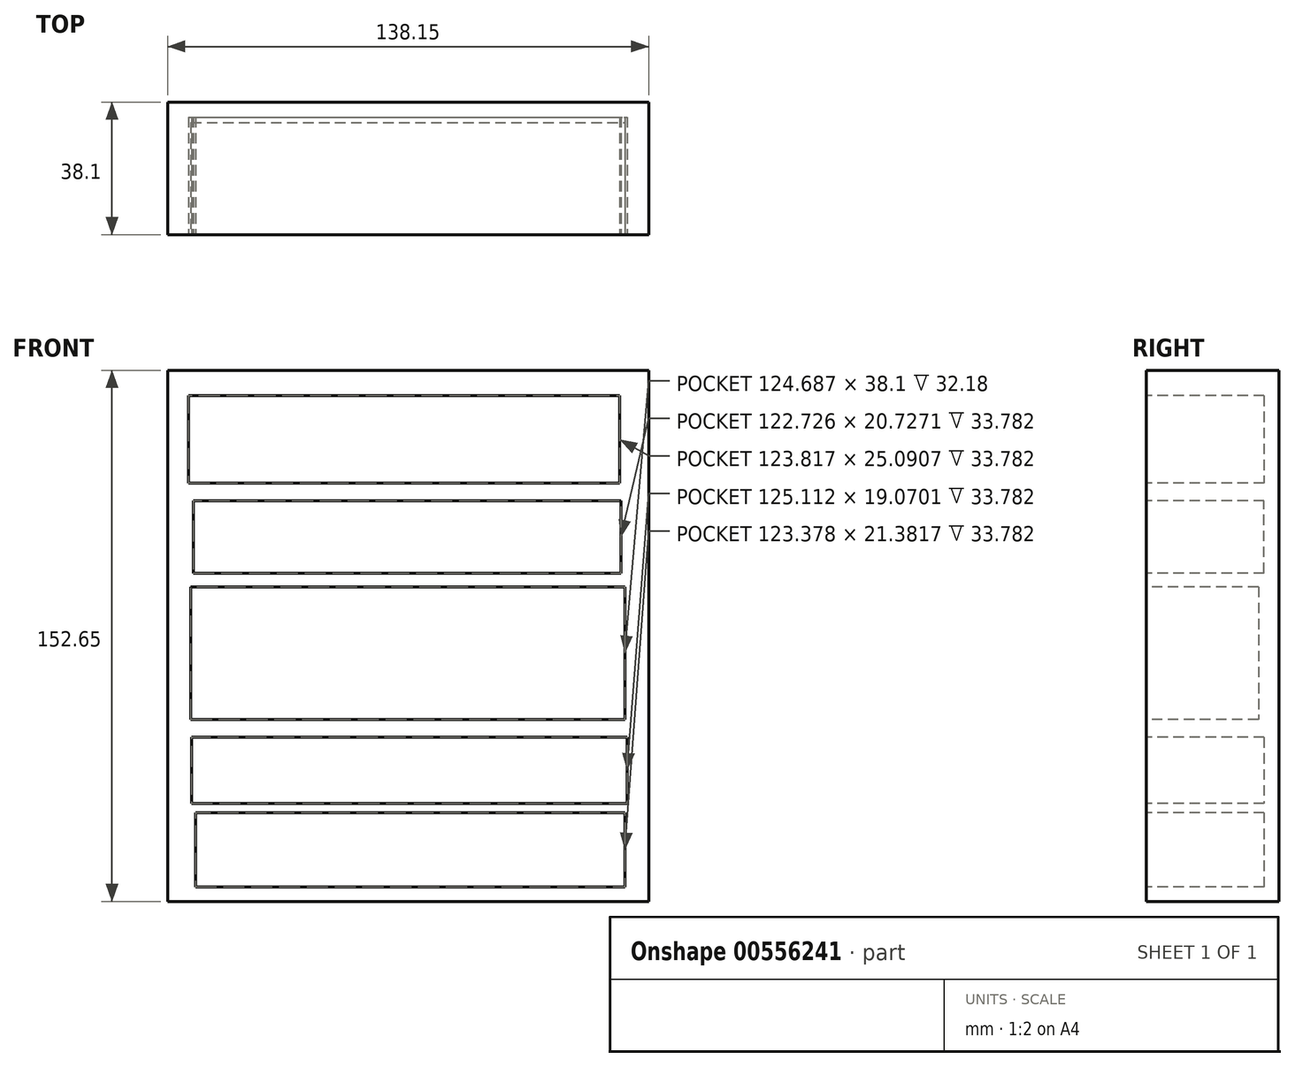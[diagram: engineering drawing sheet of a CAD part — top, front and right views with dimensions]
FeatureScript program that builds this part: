
annotation { "Feature Type Name" : "Feature", "Feature Type Description" : "" }
export const myFeature = defineFeature(function(context is Context, id is Id, definition is map)
    precondition{}
    {
        {
            var Q0;
            Q0=qCreatedBy(makeId("Front.planeOp"),FACE);
            var sketch = newSketch(context, id + "F0", { "sketchPlane" : qUnion([Q0])});
            skLineSegment(sketch, "E0.bottom", {"start": v(-68.66, 0) * mm, "end": v(69.49, 0) * mm});
            skLineSegment(sketch, "E0.top", {"start": v(-68.66, 52.32) * mm, "end": v(69.49, 52.32) * mm});
            skLineSegment(sketch, "E0.left", {"start": v(-68.66, 0) * mm, "end": v(-68.66, 52.32) * mm});
            skLineSegment(sketch, "E0.right", {"start": v(69.49, 0) * mm, "end": v(69.49, 52.32) * mm});
            skSolve(sketch);
        }
        {
            var Q0;
            Q0=makeQuery(id+"F0.imprint","IMPRINT",FACE,{"disambiguationData":[TD([[makeQuery(id+"F0.imprint","IMPRINT",EDGE,{"derivedFrom":sQuery(id+"F0.wireOp",EDGE,"E0.bottom")}),1.0]])]});
            var Q1;
            Q1 = qSketchRegion(id + "F2", true);
            extrude(context, id + "F1", {"entities" : qUnion([Q0, Q1]), "depth" : 38.1 * mm, "offsetDistance" : 25.4 * mm});
        }
        {
            var Q0;
            Q0=makeQuery(id+"F1.opExtrude","SWEPT_FACE",FACE,{"disambiguationData":[OSD([sQuery(id+"F0.wireOp",EDGE,"E0.top")])]});
            var sketch = newSketch(context, id + "F2", { "sketchPlane" : qUnion([Q0])});
            skLineSegment(sketch, "E1.bottom", {"start": v(-68.66, 0) * mm, "end": v(-61.96, 0) * mm});
            skLineSegment(sketch, "E1.top", {"start": v(-68.66, -38.1) * mm, "end": v(-61.96, -38.1) * mm});
            skLineSegment(sketch, "E1.left", {"start": v(-68.66, 0) * mm, "end": v(-68.66, -38.1) * mm});
            skLineSegment(sketch, "E1.right", {"start": v(-61.96, 0) * mm, "end": v(-61.96, -38.1) * mm});
            skLineSegment(sketch, "E2.bottom", {"start": v(69.49, 0) * mm, "end": v(62.73, 0) * mm});
            skLineSegment(sketch, "E2.top", {"start": v(69.49, -38.1) * mm, "end": v(62.73, -38.1) * mm});
            skLineSegment(sketch, "E2.left", {"start": v(69.49, 0) * mm, "end": v(69.49, -38.1) * mm});
            skLineSegment(sketch, "E2.right", {"start": v(62.73, 0) * mm, "end": v(62.73, -38.1) * mm});
            skLineSegment(sketch, "E3.bottom", {"start": v(-61.96, 0) * mm, "end": v(62.73, 0) * mm});
            skLineSegment(sketch, "E3.top", {"start": v(-61.96, -5.92) * mm, "end": v(62.73, -5.92) * mm});
            skLineSegment(sketch, "E3.left", {"start": v(-61.96, 0) * mm, "end": v(-61.96, -5.92) * mm});
            skLineSegment(sketch, "E3.right", {"start": v(62.73, 0) * mm, "end": v(62.73, -5.92) * mm});
            skSolve(sketch);
        }
        {
            var Q0;
            Q0 = qSketchRegion(id + "F2", true);
            extrude(context, id + "F3", {"entities" : qUnion([Q0]), "operationType" : NewBodyOperationType.ADD, "depth" : 38.1 * mm, "offsetDistance" : 25.4 * mm});
        }
        {
            var Q0;
            Q0=makeQuery(id+"F3.opExtrude","CAP_FACE",FACE,{"disambiguationData":[OSD([sQuery(id+"F2.wireOp",EDGE,"E1.bottom"),sQuery(id+"F2.wireOp",EDGE,"E1.top"),sQuery(id+"F2.wireOp",EDGE,"E1.left"),sQuery(id+"F2.wireOp",EDGE,"E1.right"),sQuery(id+"F2.wireOp",EDGE,"E2.bottom"),sQuery(id+"F2.wireOp",EDGE,"E2.top"),sQuery(id+"F2.wireOp",EDGE,"E2.left"),sQuery(id+"F2.wireOp",EDGE,"E2.right"),sQuery(id+"F2.wireOp",EDGE,"E3.bottom"),sQuery(id+"F2.wireOp",EDGE,"E3.top")])],"isStart":false});
            var sketch = newSketch(context, id + "F4", { "sketchPlane" : qUnion([Q0])});
            skLineSegment(sketch, "E4.bottom", {"start": v(-68.66, 0) * mm, "end": v(69.49, 0) * mm});
            skLineSegment(sketch, "E4.top", {"start": v(-68.66, -38.1) * mm, "end": v(69.49, -38.1) * mm});
            skLineSegment(sketch, "E4.left", {"start": v(-68.66, 0) * mm, "end": v(-68.66, -38.1) * mm});
            skLineSegment(sketch, "E4.right", {"start": v(69.49, 0) * mm, "end": v(69.49, -38.1) * mm});
            skSolve(sketch);
        }
        {
            var Q0;
            Q0 = qSketchRegion(id + "F4", true);
            extrude(context, id + "F5", {"entities" : qUnion([Q0]), "operationType" : NewBodyOperationType.ADD, "depth" : 2.54 * mm, "offsetDistance" : 25.4 * mm});
        }
        {
            var Q0;
            Q0=makeQuery(id+"F5.opExtrude","CAP_FACE",FACE,{"disambiguationData":[OSD([sQuery(id+"F4.wireOp",EDGE,"E4.bottom"),sQuery(id+"F4.wireOp",EDGE,"E4.top"),sQuery(id+"F4.wireOp",EDGE,"E4.left"),sQuery(id+"F4.wireOp",EDGE,"E4.right")])],"isStart":false});
            var sketch = newSketch(context, id + "F6", { "sketchPlane" : qUnion([Q0])});
            skLineSegment(sketch, "E5.bottom", {"start": v(-68.66, 0) * mm, "end": v(69.49, 0) * mm});
            skLineSegment(sketch, "E5.top", {"start": v(-68.66, -38.1) * mm, "end": v(69.49, -38.1) * mm});
            skLineSegment(sketch, "E5.left", {"start": v(-68.66, 0) * mm, "end": v(-68.66, -38.1) * mm});
            skLineSegment(sketch, "E5.right", {"start": v(69.49, 0) * mm, "end": v(69.49, -38.1) * mm});
            skSolve(sketch);
        }
        {
            var Q0;
            Q0 = qSketchRegion(id + "F6", true);
            extrude(context, id + "F7", {"entities" : qUnion([Q0]), "operationType" : NewBodyOperationType.ADD, "depth" : 59.69 * mm, "offsetDistance" : 25.4 * mm});
        }
        {
            var Q0;
            Q0=makeQuery(id+"F7.boolean.opBoolean","MERGE",FACE,{"derivedFrom":[makeQuery(id+"F5.boolean.opBoolean","MERGE",FACE,{"derivedFrom":[makeQuery(id+"F3.boolean.opBoolean","MERGE",FACE,{"derivedFrom":[makeQuery(id+"F1.opExtrude","CAP_FACE",FACE,{"disambiguationData":[OSD([sQuery(id+"F0.wireOp",EDGE,"E0.bottom"),sQuery(id+"F0.wireOp",EDGE,"E0.top"),sQuery(id+"F0.wireOp",EDGE,"E0.left"),sQuery(id+"F0.wireOp",EDGE,"E0.right")])],"isStart":false}),makeQuery(id+"F3.opExtrude","SWEPT_FACE",FACE,{"disambiguationData":[OSD([sQuery(id+"F2.wireOp",EDGE,"E1.top")])]}),makeQuery(id+"F3.opExtrude","SWEPT_FACE",FACE,{"disambiguationData":[OSD([sQuery(id+"F2.wireOp",EDGE,"E2.top")])]})]}),makeQuery(id+"F5.opExtrude","SWEPT_FACE",FACE,{"disambiguationData":[OSD([sQuery(id+"F4.wireOp",EDGE,"E4.top")])]})]}),makeQuery(id+"F7.opExtrude","SWEPT_FACE",FACE,{"disambiguationData":[OSD([sQuery(id+"F6.wireOp",EDGE,"E5.top")])]})]});
            var sketch = newSketch(context, id + "F8", { "sketchPlane" : qUnion([Q0])});
            skLineSegment(sketch, "E6.bottom", {"start": v(-61.24, 94.35) * mm, "end": v(61.49, 94.35) * mm});
            skLineSegment(sketch, "E6.top", {"start": v(-61.24, 115.08) * mm, "end": v(61.49, 115.08) * mm});
            skLineSegment(sketch, "E6.left", {"start": v(-61.24, 94.35) * mm, "end": v(-61.24, 115.08) * mm});
            skLineSegment(sketch, "E6.right", {"start": v(61.49, 94.35) * mm, "end": v(61.49, 115.08) * mm});
            skSolve(sketch);
        }
        {
            var Q0;
            Q0=makeQuery(id+"F8.imprint","IMPRINT",FACE,{"disambiguationData":[TD([[makeQuery(id+"F8.imprint","IMPRINT",EDGE,{"derivedFrom":sQuery(id+"F8.wireOp",EDGE,"E6.bottom")}),-1.0]])]});
            var sketch = newSketch(context, id + "F9", { "sketchPlane" : qUnion([Q0])});
            skLineSegment(sketch, "E7.bottom", {"start": v(-62.6, 145.35) * mm, "end": v(61.21, 145.35) * mm});
            skLineSegment(sketch, "E7.top", {"start": v(-62.6, 120.26) * mm, "end": v(61.21, 120.26) * mm});
            skLineSegment(sketch, "E7.left", {"start": v(-62.6, 145.35) * mm, "end": v(-62.6, 120.26) * mm});
            skLineSegment(sketch, "E7.right", {"start": v(61.21, 145.35) * mm, "end": v(61.21, 120.26) * mm});
            skSolve(sketch);
        }
        {
            var Q0;
            Q0=makeQuery(id+"F8.imprint","IMPRINT",FACE,{"disambiguationData":[TD([[makeQuery(id+"F8.imprint","IMPRINT",EDGE,{"derivedFrom":sQuery(id+"F8.wireOp",EDGE,"E6.bottom")}),-1.0]])]});
            var sketch = newSketch(context, id + "F10", { "sketchPlane" : qUnion([Q0])});
            skLineSegment(sketch, "E8.bottom", {"start": v(-61.8, 47.18) * mm, "end": v(63.3, 47.18) * mm});
            skLineSegment(sketch, "E8.top", {"start": v(-61.8, 28.1) * mm, "end": v(63.3, 28.1) * mm});
            skLineSegment(sketch, "E8.left", {"start": v(-61.8, 47.18) * mm, "end": v(-61.8, 28.1) * mm});
            skLineSegment(sketch, "E8.right", {"start": v(63.3, 47.18) * mm, "end": v(63.3, 28.1) * mm});
            skSolve(sketch);
        }
        {
            var Q0;
            Q0=makeQuery(id+"F8.imprint","IMPRINT",FACE,{"disambiguationData":[TD([[makeQuery(id+"F8.imprint","IMPRINT",EDGE,{"derivedFrom":sQuery(id+"F8.wireOp",EDGE,"E6.bottom")}),-1.0]])]});
            var sketch = newSketch(context, id + "F11", { "sketchPlane" : qUnion([Q0])});
            skLineSegment(sketch, "E9.bottom", {"start": v(-60.65, 25.5) * mm, "end": v(62.73, 25.5) * mm});
            skLineSegment(sketch, "E9.top", {"start": v(-60.65, 4.13) * mm, "end": v(62.73, 4.13) * mm});
            skLineSegment(sketch, "E9.left", {"start": v(-60.65, 25.5) * mm, "end": v(-60.65, 4.13) * mm});
            skLineSegment(sketch, "E9.right", {"start": v(62.73, 25.5) * mm, "end": v(62.73, 4.13) * mm});
            skSolve(sketch);
        }
        {
            var Q0;
            Q0 = qSketchRegion(id + "F8", true);
            extrude(context, id + "F12", {"entities" : qUnion([Q0]), "operationType" : NewBodyOperationType.REMOVE, "oppositeDirection" : true, "depth" : 33.78 * mm, "offsetDistance" : 25.4 * mm});
        }
        {
            var Q0;
            Q0=makeQuery(id+"F9.imprint","IMPRINT",FACE,{"disambiguationData":[TD([[makeQuery(id+"F9.imprint","IMPRINT",EDGE,{"derivedFrom":sQuery(id+"F9.wireOp",EDGE,"E7.bottom")}),-1.0]])]});
            extrude(context, id + "F13", {"entities" : qUnion([Q0]), "operationType" : NewBodyOperationType.REMOVE, "oppositeDirection" : true, "depth" : 33.78 * mm, "offsetDistance" : 25.4 * mm});
        }
        {
            var Q0;
            Q0 = qSketchRegion(id + "F10", true);
            extrude(context, id + "F14", {"entities" : qUnion([Q0]), "operationType" : NewBodyOperationType.REMOVE, "oppositeDirection" : true, "depth" : 33.78 * mm, "offsetDistance" : 25.4 * mm});
        }
        {
            var Q0;
            Q0=makeQuery(id+"F11.imprint","IMPRINT",FACE,{"disambiguationData":[TD([[makeQuery(id+"F11.imprint","IMPRINT",EDGE,{"derivedFrom":sQuery(id+"F11.wireOp",EDGE,"E9.bottom")}),-1.0]])]});
            extrude(context, id + "F15", {"entities" : qUnion([Q0]), "operationType" : NewBodyOperationType.REMOVE, "oppositeDirection" : true, "depth" : 33.78 * mm, "offsetDistance" : 25.4 * mm});
        }
    });
